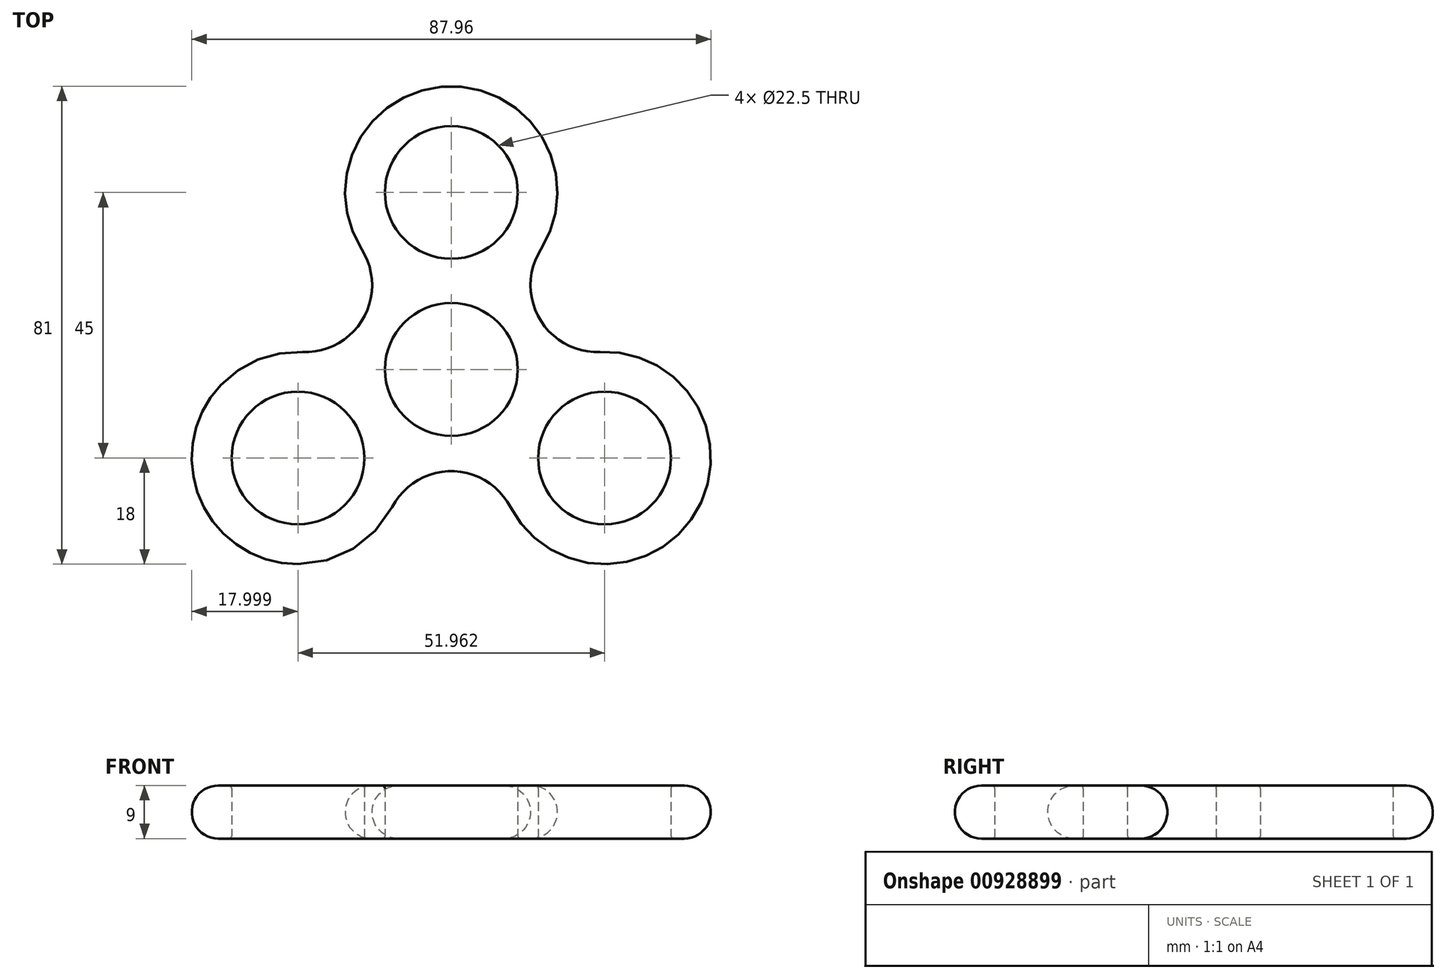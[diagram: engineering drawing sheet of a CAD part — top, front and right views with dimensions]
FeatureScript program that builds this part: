
annotation { "Feature Type Name" : "Feature", "Feature Type Description" : "" }
export const myFeature = defineFeature(function(context is Context, id is Id, definition is map)
    precondition{}
    {
        {
            var Q0;
            Q0=qCreatedBy(makeId("Top.planeOp"),FACE);
            var sketch = newSketch(context, id + "F0", { "sketchPlane" : qUnion([Q0])});
            skCircle(sketch, "E0", {"center": v(0, 0) * mm, "radius": 11.25 * mm});
            skCircle(sketch, "E1", {"center": v(0, 30) * mm, "radius": 11.25 * mm});
            skCircle(sketch, "E2", {"center": v(25.98, -15) * mm, "radius": 11.25 * mm});
            skCircle(sketch, "E3", {"center": v(-25.98, -15) * mm, "radius": 11.25 * mm});
            skLineSegment(sketch, "E4", {"start": v(0, 0) * mm, "end": v(0, 30) * mm});
            skLineSegment(sketch, "E5", {"start": v(0, 0) * mm, "end": v(25.98, -15) * mm});
            skLineSegment(sketch, "E6", {"start": v(0, 0) * mm, "end": v(-25.98, -15) * mm});
            skCircle(sketch, "E7", {"center": v(-25.98, -15) * mm, "radius": 18 * mm});
            skCircle(sketch, "E8", {"center": v(25.98, -15) * mm, "radius": 18 * mm});
            skCircle(sketch, "E9", {"center": v(0, 30) * mm, "radius": 18 * mm});
            skCircle(sketch, "E10", {"center": v(-24.73, 14.28) * mm, "radius": 11.3 * mm});
            skCircle(sketch, "E11", {"center": v(24.73, 14.28) * mm, "radius": 11.3 * mm});
            skCircle(sketch, "E12", {"center": v(0, -28.55) * mm, "radius": 11.3 * mm});
            skSolve(sketch);
        }
        {
            var Q0;
            {var subQ5=sQuery(id+"F0.wireOp",EDGE,"E0");var subQ8=sQuery(id+"F0.wireOp",EDGE,"E4");var subQ10=makeQuery(id+"F0.imprint","INTERSECT",VERTEX,{"derivedFrom":[subQ5,subQ8]});Q0=makeQuery(id+"F0.imprint","IMPRINT",FACE,{"disambiguationData":[TD([[makeQuery(id+"F0.imprint","IMPRINT",EDGE,{"disambiguationData":[TD([[subQ10,1.0]])],"derivedFrom":subQ5}),-1.0]])]});}
            var Q1;
            {var subQ1=sQuery(id+"F0.wireOp",EDGE,"E6");var subQ3=sQuery(id+"F0.wireOp",EDGE,"E0");var subQ4=makeQuery(id+"F0.imprint","INTERSECT",VERTEX,{"derivedFrom":[subQ3,subQ1]});Q1=makeQuery(id+"F0.imprint","IMPRINT",FACE,{"disambiguationData":[TD([[makeQuery(id+"F0.imprint","IMPRINT",EDGE,{"disambiguationData":[TD([[subQ4,1.0]])],"derivedFrom":subQ3}),-1.0]])]});}
            var Q2;
            {var subQ1=sQuery(id+"F0.wireOp",EDGE,"E6");var subQ9=sQuery(id+"F0.wireOp",EDGE,"E0");var subQ11=makeQuery(id+"F0.imprint","INTERSECT",VERTEX,{"derivedFrom":[subQ9,subQ1]});Q2=makeQuery(id+"F0.imprint","IMPRINT",FACE,{"disambiguationData":[TD([[makeQuery(id+"F0.imprint","IMPRINT",EDGE,{"disambiguationData":[TD([[subQ11,-1.0]])],"derivedFrom":subQ9}),-1.0]])]});}
            var Q3;
            Q3=makeQuery(id+"F0.imprint","IMPRINT",FACE,{"disambiguationData":[TD([[makeQuery(id+"F0.imprint","IMPRINT",EDGE,{"derivedFrom":sQuery(id+"F0.wireOp",EDGE,"E3")}),-1.0]])]});
            var Q4;
            Q4=makeQuery(id+"F0.imprint","IMPRINT",FACE,{"disambiguationData":[TD([[makeQuery(id+"F0.imprint","IMPRINT",EDGE,{"derivedFrom":sQuery(id+"F0.wireOp",EDGE,"E2")}),-1.0]])]});
            var Q5;
            Q5=makeQuery(id+"F0.imprint","IMPRINT",FACE,{"disambiguationData":[TD([[makeQuery(id+"F0.imprint","IMPRINT",EDGE,{"derivedFrom":sQuery(id+"F0.wireOp",EDGE,"E1")}),-1.0]])]});
            extrude(context, id + "F1", {"entities" : qUnion([Q0, Q1, Q2, Q3, Q4, Q5]), "depth" : 9 * mm, "offsetDistance" : 25 * mm});
        }
        {
            var Q0;
            Q0=makeQuery(id+"F1.opExtrude","SWEPT_FACE",FACE,{"disambiguationData":[OSD([sQuery(id+"F0.wireOp",EDGE,"E10")])]});
            var Q1;
            Q1=makeQuery(id+"F1.opExtrude","SWEPT_FACE",FACE,{"disambiguationData":[OSD([sQuery(id+"F0.wireOp",EDGE,"E9")])]});
            fillet(context, id + "F2", {"entities" : qUnion([Q0, Q1]), "radius" : 4.5 * mm, "tangentPropagation" : true, "allowEdgeOverflow" : false});
        }
        {
            var Q0;
            Q0=makeQuery(id+"F1.opExtrude","SWEPT_FACE",FACE,{"disambiguationData":[OSD([sQuery(id+"F0.wireOp",EDGE,"E0")])]});
            var Q1;
            Q1=makeQuery(id+"F1.opExtrude","SWEPT_FACE",FACE,{"disambiguationData":[OSD([sQuery(id+"F0.wireOp",EDGE,"E3")])]});
            var Q2;
            Q2=makeQuery(id+"F1.opExtrude","SWEPT_FACE",FACE,{"disambiguationData":[OSD([sQuery(id+"F0.wireOp",EDGE,"E2")])]});
            var Q3;
            Q3=makeQuery(id+"F1.opExtrude","SWEPT_FACE",FACE,{"disambiguationData":[OSD([sQuery(id+"F0.wireOp",EDGE,"E1")])]});
            fillet(context, id + "F3", {"entities" : qUnion([Q0, Q1, Q2, Q3]), "radius" : 0.5 * mm, "tangentPropagation" : true, "allowEdgeOverflow" : false});
        }
    });
